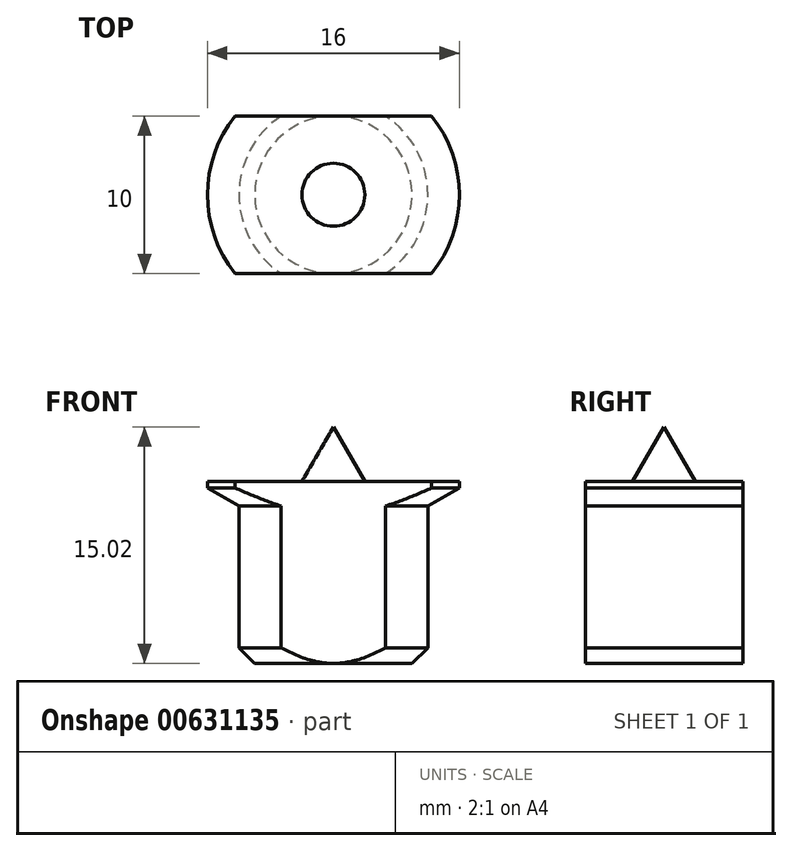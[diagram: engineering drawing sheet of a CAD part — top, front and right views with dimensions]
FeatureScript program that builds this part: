
annotation { "Feature Type Name" : "Feature", "Feature Type Description" : "" }
export const myFeature = defineFeature(function(context is Context, id is Id, definition is map)
    precondition{}
    {
        {
            var Q0;
            Q0=qCreatedBy(makeId("Front.planeOp"),FACE);
            var sketch = newSketch(context, id + "F0", { "sketchPlane" : qUnion([Q0])});
            skLineSegment(sketch, "E0", {"start": v(0, -10) * mm, "end": v(-5, -10) * mm});
            skLineSegment(sketch, "E1", {"start": v(-5, -10) * mm, "end": v(-6, -9) * mm});
            skLineSegment(sketch, "E2", {"start": v(-6, -9) * mm, "end": v(-6, 0) * mm});
            skLineSegment(sketch, "E3", {"start": v(-6, 0) * mm, "end": v(-8, 1.15) * mm});
            skLineSegment(sketch, "E4", {"start": v(-8, 1.15) * mm, "end": v(-8, 1.55) * mm});
            skLineSegment(sketch, "E5", {"start": v(-8, 1.55) * mm, "end": v(-2, 1.55) * mm});
            skLineSegment(sketch, "E6", {"start": v(-2, 1.55) * mm, "end": v(0, 5.02) * mm});
            skLineSegment(sketch, "E7", {"start": v(0, 5.02) * mm, "end": v(0, -10) * mm});
            skSolve(sketch);
        }
        {
            var Q0;
            Q0=makeQuery(id+"F0.imprint","IMPRINT",FACE,{"disambiguationData":[TD([[makeQuery(id+"F0.imprint","IMPRINT",EDGE,{"derivedFrom":sQuery(id+"F0.wireOp",EDGE,"E0")}),-1.0]])]});
            var Q1;
            Q1=sQuery(id+"F0.wireOp",EDGE,"E7");
            revolve(context, id + "F1", {"entities" : qUnion([Q0]), "axis" : qUnion([Q1]), "revolveType" : RevolveType.FULL});
        }
        {
            var Q0;
            Q0=qCreatedBy(makeId("Top.planeOp"),FACE);
            var sketch = newSketch(context, id + "F2", { "sketchPlane" : qUnion([Q0])});
            skLineSegment(sketch, "E8.bottom", {"start": v(-9.78, -5) * mm, "end": v(10.99, -5) * mm});
            skLineSegment(sketch, "E8.top", {"start": v(-9.78, 5) * mm, "end": v(10.99, 5) * mm});
            skLineSegment(sketch, "E8.left", {"start": v(-9.78, -5) * mm, "end": v(-9.78, 5) * mm});
            skLineSegment(sketch, "E8.right", {"start": v(10.99, -5) * mm, "end": v(10.99, 5) * mm});
            skSolve(sketch);
        }
        {
            var Q0;
            Q0=makeQuery(id+"F2.imprint","IMPRINT",FACE,{"disambiguationData":[TD([[makeQuery(id+"F2.imprint","IMPRINT",EDGE,{"derivedFrom":sQuery(id+"F2.wireOp",EDGE,"E8.bottom")}),1.0]])]});
            extrude(context, id + "F3", {"entities" : qUnion([Q0]), "operationType" : NewBodyOperationType.INTERSECT, "depth" : 25 * mm, "offsetDistance" : 25 * mm, "hasSecondDirection" : true, "secondDirectionOppositeDirection" : true, "secondDirectionDepth" : 25 * mm});
        }
    });
